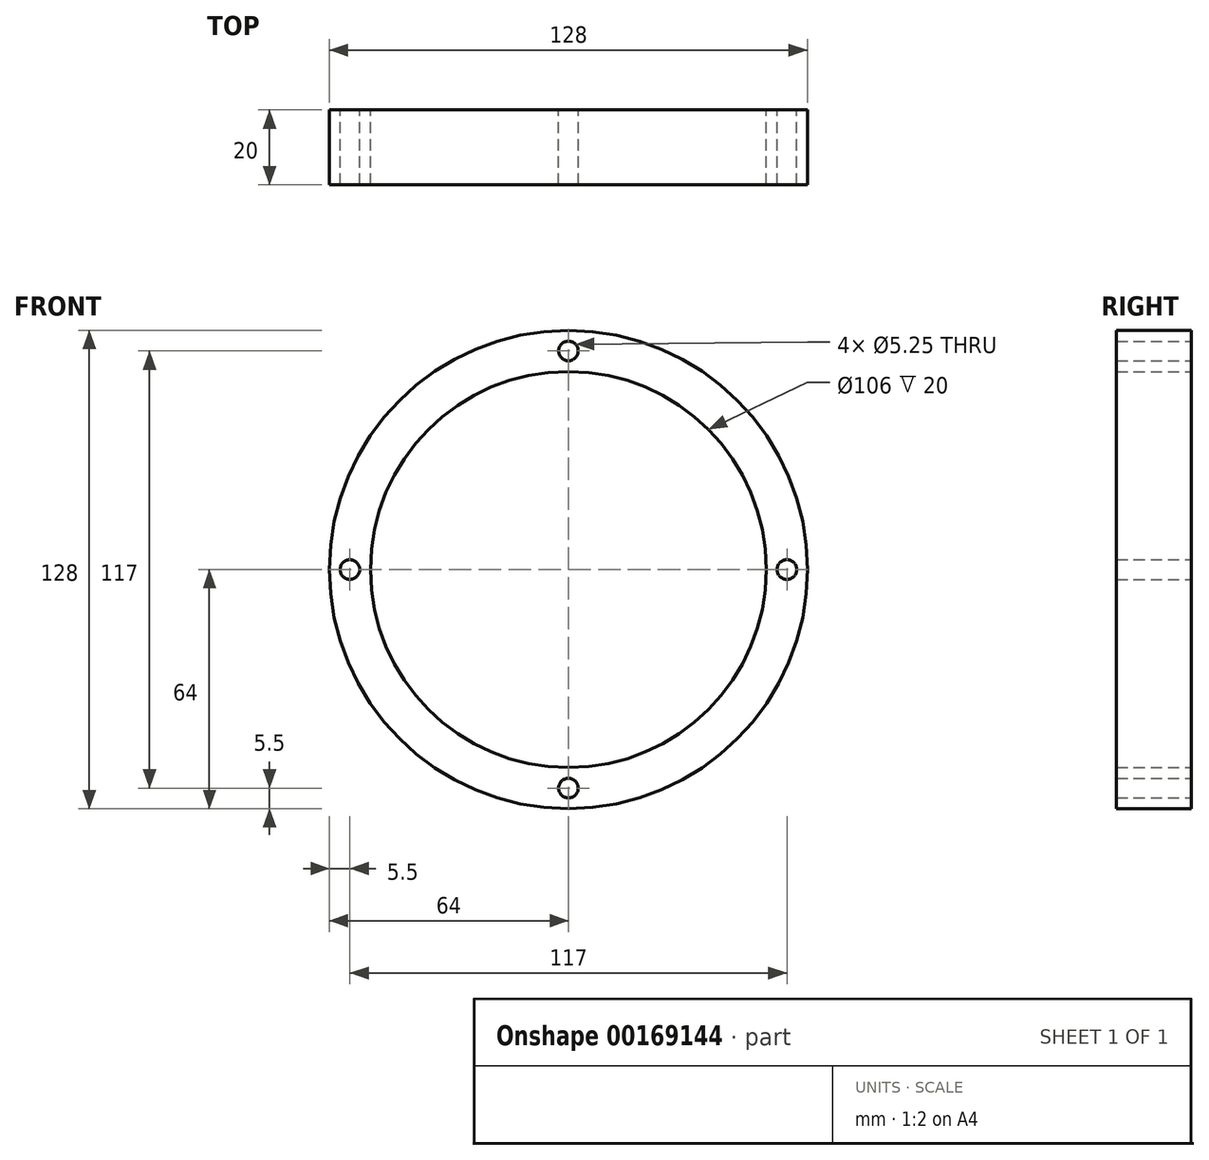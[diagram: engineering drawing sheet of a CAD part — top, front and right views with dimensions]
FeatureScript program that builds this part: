
annotation { "Feature Type Name" : "Feature", "Feature Type Description" : "" }
export const myFeature = defineFeature(function(context is Context, id is Id, definition is map)
    precondition{}
    {
        {
            var Q0;
            Q0=qCreatedBy(makeId("Front.planeOp"),FACE);
            var sketch = newSketch(context, id + "F0", { "sketchPlane" : qUnion([Q0])});
            skCircle(sketch, "E0", {"center": v(0, 0) * mm, "radius": 64 * mm});
            skCircle(sketch, "E1", {"center": v(0, 0) * mm, "radius": 53 * mm});
            skLineSegment(sketch, "E2", {"start": v(0, 0) * mm, "end": v(0, 74.07) * mm, "construction": true});
            skCircle(sketch, "E3.0", {"center": v(0, 0) * mm, "radius": 58.5 * mm, "construction": true});
            skCircle(sketch, "E4", {"center": v(0, 58.5) * mm, "radius": 2.62 * mm});
            skCircle(sketch, "E5.1.0", {"center": v(-58.5, 0) * mm, "radius": 2.62 * mm});
            skCircle(sketch, "E5.2.0", {"center": v(0, -58.5) * mm, "radius": 2.62 * mm});
            skCircle(sketch, "E6.1.3.0", {"center": v(58.5, 0) * mm, "radius": 2.62 * mm});
            skSolve(sketch);
        }
        {
            var Q0;
            Q0 = qSketchRegion(id + "F0", true);
            extrude(context, id + "F1", {"entities" : qUnion([Q0]), "depth" : 20 * mm});
        }
    });
